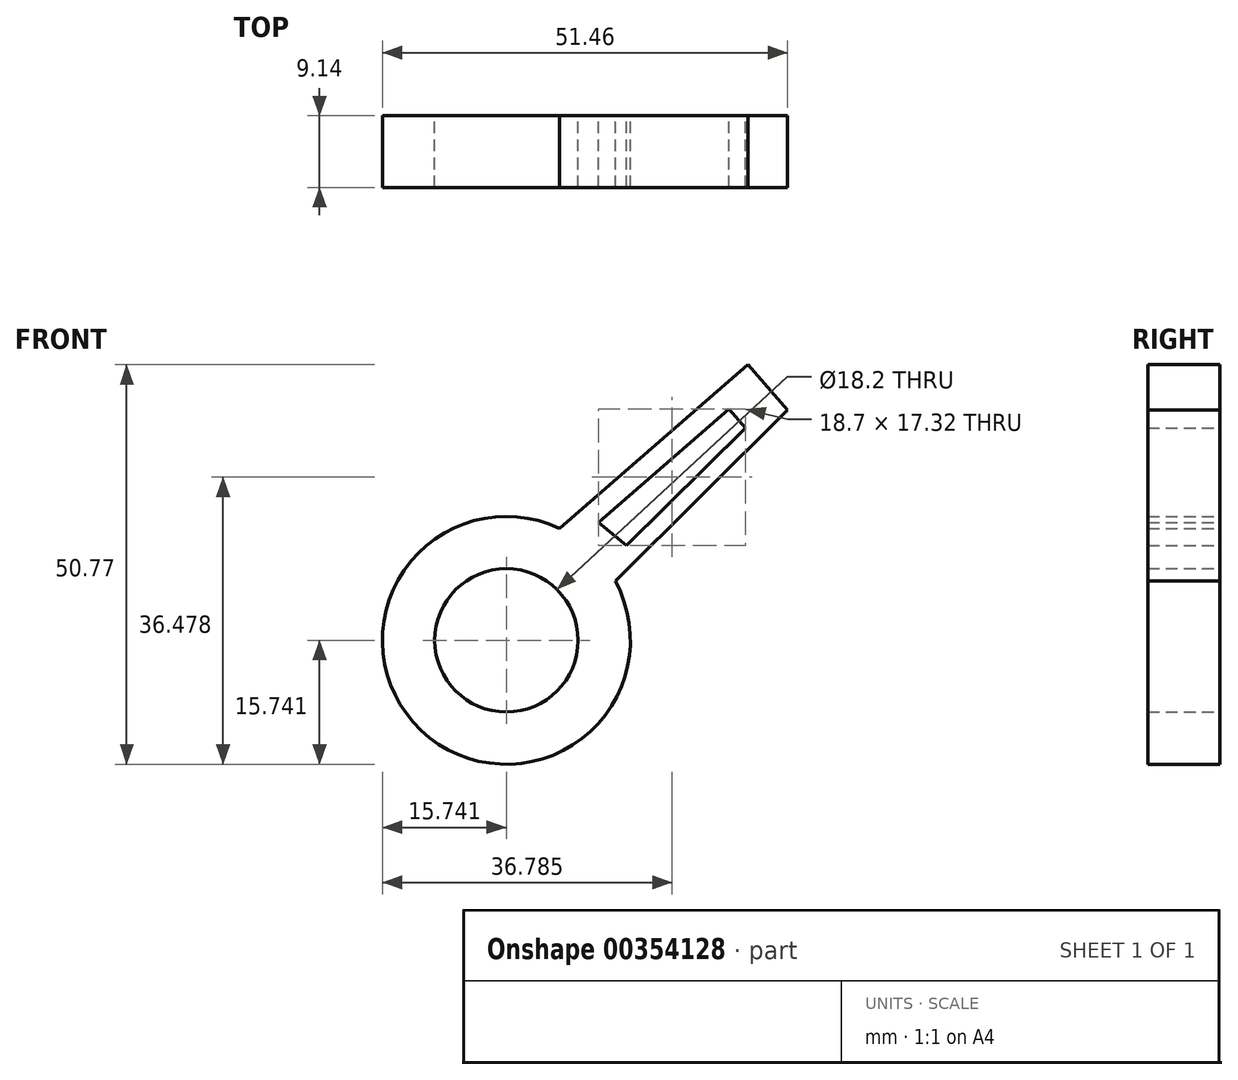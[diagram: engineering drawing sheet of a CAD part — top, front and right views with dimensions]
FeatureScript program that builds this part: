
annotation { "Feature Type Name" : "Feature", "Feature Type Description" : "" }
export const myFeature = defineFeature(function(context is Context, id is Id, definition is map)
    precondition{}
    {
        {
            var Q0;
            Q0=qCreatedBy(makeId("Front.planeOp"),FACE);
            var sketch = newSketch(context, id + "F0", { "sketchPlane" : qUnion([Q0])});
            skCircle(sketch, "E0.MirrorC", {"center": v(-26.66, -31) * mm, "radius": 15.75 * mm});
            skLineSegment(sketch, "E1.MirrorCS", {"start": v(5.3, -6.63) * mm, "end": v(-15.15, -26.1) * mm});
            skLineSegment(sketch, "E2.MirrorCS", {"start": v(2.69, 1.52) * mm, "end": v(-22.05, -19.77) * mm});
            skCircle(sketch, "E3.MirrorC", {"center": v(-26.66, -31) * mm, "radius": 9.1 * mm});
            skSolve(sketch);
        }
        {
            var Q0;
            Q0=makeQuery(id+"F0.imprint","IMPRINT",FACE,{"disambiguationData":[TD([[makeQuery(id+"F0.imprint","IMPRINT",EDGE,{"derivedFrom":sQuery(id+"F0.wireOp",EDGE,"E0.MirrorC")}),1.0]])]});
            extrude(context, id + "F1", {"entities" : qUnion([Q0]), "depth" : 9.14 * mm});
        }
        {
            var Q0;
            Q0=qCreatedBy(makeId("Front.planeOp"),FACE);
            var sketch = newSketch(context, id + "F2", { "sketchPlane" : qUnion([Q0])});
            skLineSegment(sketch, "E4", {"start": v(-22.45, -19) * mm, "end": v(4.03, 4.03) * mm});
            skLineSegment(sketch, "E5", {"start": v(4.03, 4.03) * mm, "end": v(9.06, -1.76) * mm});
            skLineSegment(sketch, "E6", {"start": v(9.06, -1.76) * mm, "end": v(-14.4, -25.04) * mm});
            skLineSegment(sketch, "E7", {"start": v(-14.4, -25.04) * mm, "end": v(-22.45, -19) * mm});
            skLineSegment(sketch, "E8", {"start": v(-14.96, -16.01) * mm, "end": v(1.6, -1.6) * mm});
            skLineSegment(sketch, "E9", {"start": v(1.6, -1.6) * mm, "end": v(3.73, -4.05) * mm});
            skLineSegment(sketch, "E10", {"start": v(3.73, -4.05) * mm, "end": v(-11.42, -18.92) * mm});
            skLineSegment(sketch, "E11", {"start": v(-11.42, -18.92) * mm, "end": v(-14.96, -16.01) * mm});
            skSolve(sketch);
        }
        {
            var Q0;
            Q0=qSketchRegion(id+"F2",true);
            extrude(context, id + "F3", {"entities" : qUnion([Q0]), "operationType" : NewBodyOperationType.ADD, "depth" : 9.14 * mm});
        }
    });
